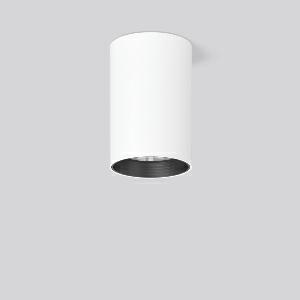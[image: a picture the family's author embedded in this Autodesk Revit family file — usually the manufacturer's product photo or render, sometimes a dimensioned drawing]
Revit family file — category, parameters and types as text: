
# Revit family: heledon_maxi_a_931221_002_2_76_18ef
name_source: partatom
category: Lighting Fixtures
units: mm (PartAtom-declared; Revit-internal decimal feet)

## family parameters
Cut with Voids When Loaded = No
Host = Face
Light Source = No
Part Type = Normal
Room Calculation Point = No
Round Connector Dimension = Use Diameter
Shared = No

## types (1)
- HELEDON maxi A (1 x LED Modul 927, 2550 lm, 2700)
    Apparent Load = 25 VA
    Approval mark = CE
    CIE Flux Codes = 96 100 100 100 100
    Color Rendering = 92
    Color Temperature = 2700
    Default Elevation = 1800 mm
    Description = Series: HELEDON maxi
Cylindrical surface-mounted downlight. Housing: die-cast aluminium, powder-coated. Internal ceiling frame polycarbonate with bayonet mounting. Black plastic ring and recessed LED to prevent glare from the side. Optical assembly with lens made of plastic (polycarbonate) for the best homogeneous light distribution - can be changed without tools. Best colour rendering index Ra>90. Suitable for Ceiling mounting. Easy installation with a separate ceiling frame with bayonet mounting and plug connection. Driver integrated. Connected via plug-in connector. High quality converter without flickering and stroboscopic effect. The following accessories can be mounted without use of tools: interchangeable lenses, decorative glasses, honeycomb louvre, clear and frosted diffusers, white interchangeable plastic ring. 
Colour: traffic white, matt (RAL 9016)
Diameter: 123 mm
Height: 183 mm
Lamp: LED
Socket: without socket
Colour temperature: 2700K
Colour rendering index (CRI): 92
System power: 25 W
Rated luminous flux: 2550 lm
Luminous efficiency: 102 lm/W
Control gear: Converter, dimmable, DALI
Protection class: I
Type of protection: IP 20
    Height = 183 mm
    Lamp = 1 x LED Modul 927
    Lamp Light Flux = 2550 lm
    Lamp count = 1
    Length = 123 mm
    Lifetime = 50000 h
    Luminous efficacy = 102 lm/W
    Manufacturer = RZB
    ModVariant = No
    Model = 931221.002.2.76
    Mounting Place = Ceiling
    Mounting Type = Surface mounted
    Number of Poles = 1
    OnlyDefault = Yes
    Power Factor = 1
    Product Name = HELEDON maxi A
    Product group = Surface mounted downlights
    ProductGroupID = 302
    Protection Class = Protection class I
    Protection Degree = IP 20
    RLX_Detail_Level = 1
    RLX_Emergency_Light_Flux = 0 lm
    RLX_Emergency_Type = 0
    RLX_Emergency_Type_DB = No
    RlxData = <blob elided: 97389 chars, md5=fff50f30>
    Socket = socket
    Standby Power = 0 W
    System Light Flux = 2550 lm
    System Power = 25 W
    Type Comments = Product without accessories
    Type Image = 931193.002.jpg
    URL = http://relux.com
    VarID = ---
    Voltage = 230 V
    Voltage Range = 220-240 V
    Weight = 0.00 kg
    Width = 0 mm  [stored 0 ft]

note: [stored X ft] marks values corroborated as IEEE doubles in the binary element streams (Revit-internal decimal feet)

## geometry (parser evidence)
native form markers: Blend x4, Sweep x9
no freeform markers — native parametric forms only
